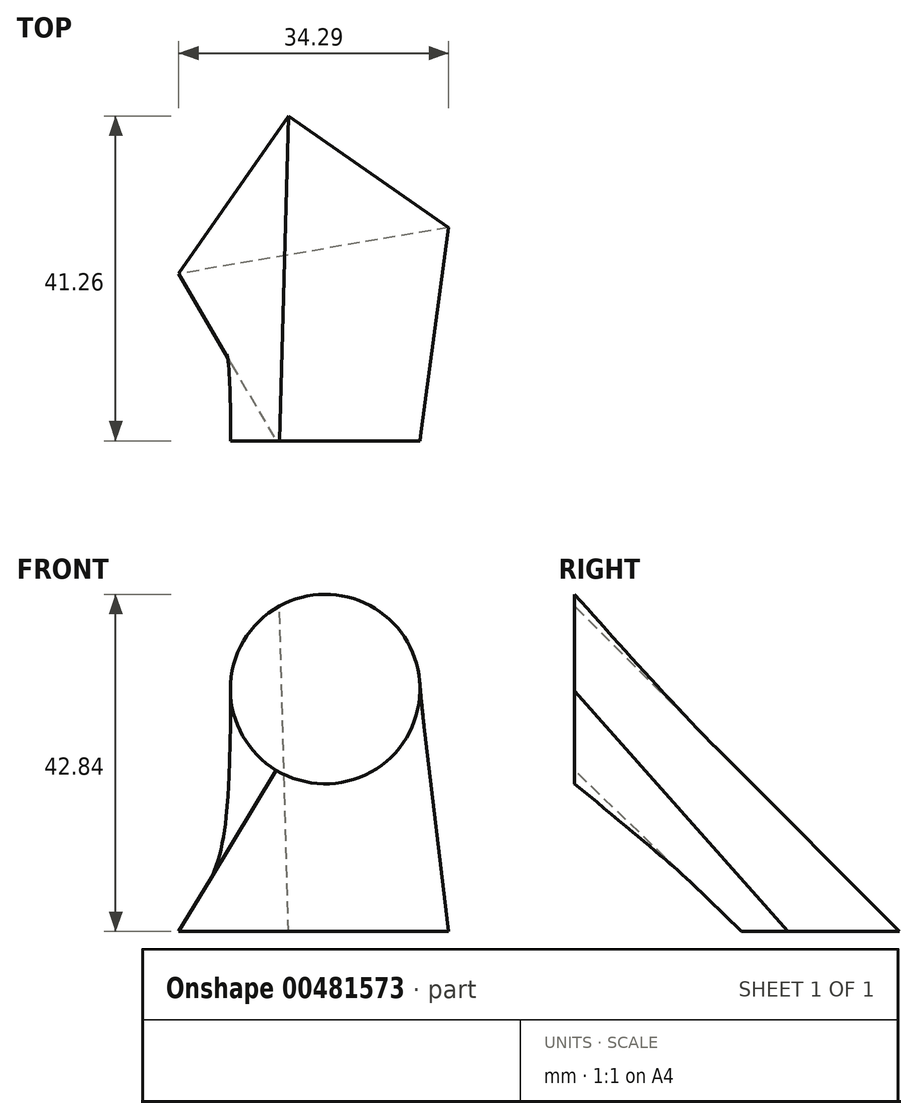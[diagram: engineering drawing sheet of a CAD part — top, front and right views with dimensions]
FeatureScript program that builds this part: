
annotation { "Feature Type Name" : "Feature", "Feature Type Description" : "" }
export const myFeature = defineFeature(function(context is Context, id is Id, definition is map)
    precondition{}
    {
        {
            var Q0;
            Q0=qCreatedBy(makeId("Top.planeOp"),FACE);
            var sketch = newSketch(context, id + "F0", { "sketchPlane" : qUnion([Q0])});
            skLineSegment(sketch, "E0", {"start": v(-58.99, 21.21) * mm, "end": v(-45.04, 41.26) * mm});
            skLineSegment(sketch, "E1", {"start": v(-45.04, 41.26) * mm, "end": v(-24.7, 27.11) * mm});
            skLineSegment(sketch, "E2", {"start": v(-24.7, 27.11) * mm, "end": v(-58.99, 21.21) * mm});
            skSolve(sketch);
        }
        {
            var Q0;
            Q0=qCreatedBy(makeId("Front.planeOp"),FACE);
            var sketch = newSketch(context, id + "F1", { "sketchPlane" : qUnion([Q0])});
            skCircle(sketch, "E3", {"center": v(-40.4, 30.8) * mm, "radius": 12.04 * mm});
            skSolve(sketch);
        }
        {
            var Q0;
            Q0 = qSketchRegion(id + "F0", true);
            var Q1;
            Q1 = qSketchRegion(id + "F1", true);
            loft(context, id + "F2", {"sheetProfilesArray" : [{ "sheetProfileEntities" : qUnion([Q0]) }, { "sheetProfileEntities" : qUnion([Q1]) }]});
        }
    });
